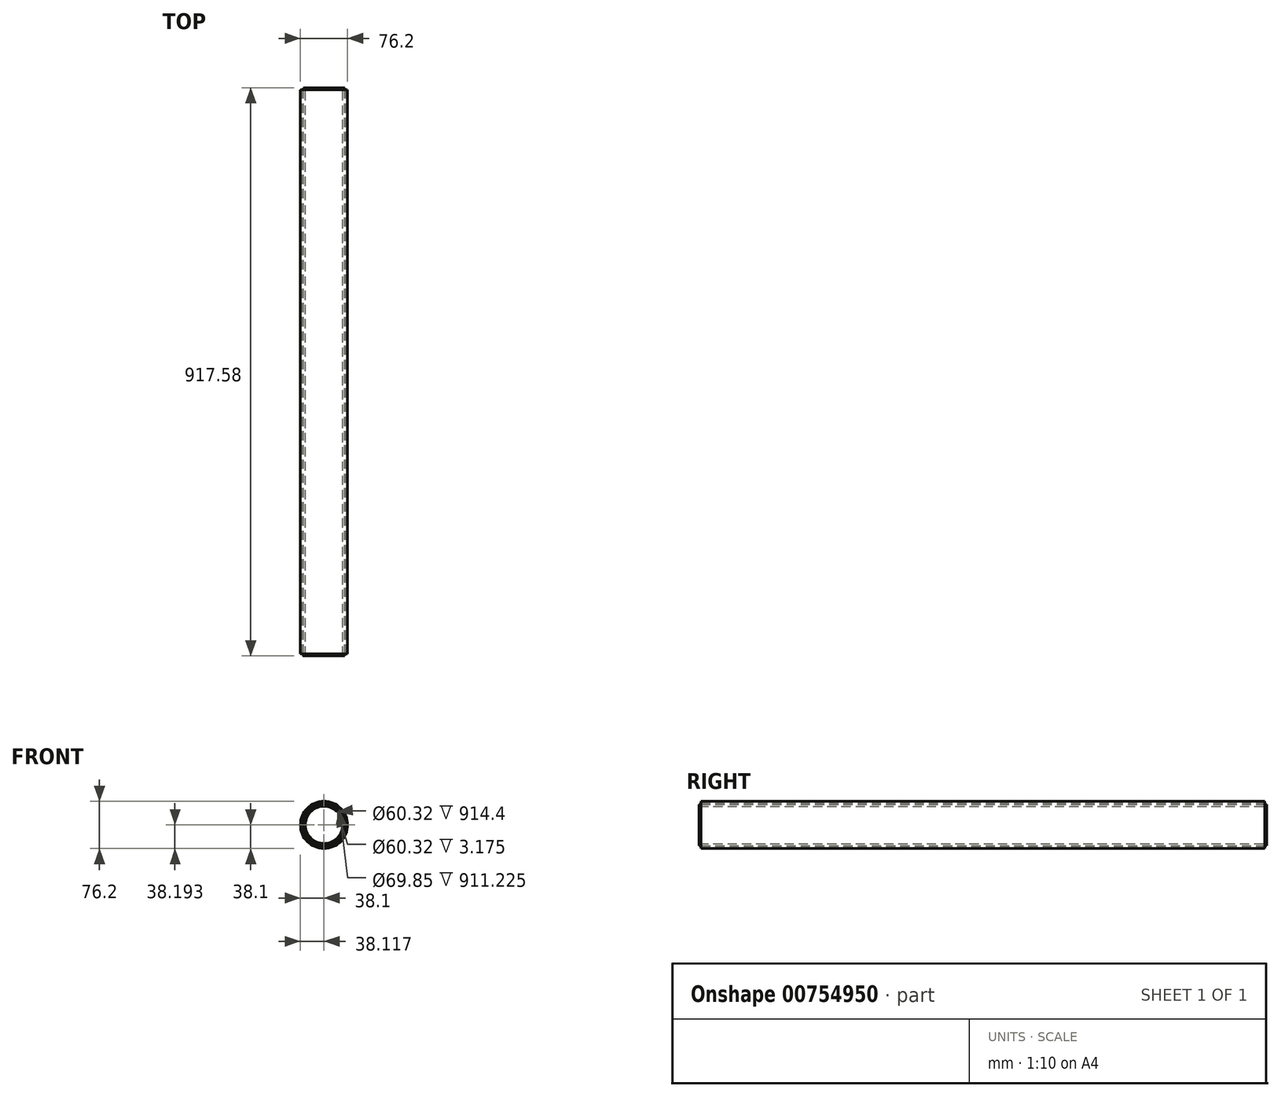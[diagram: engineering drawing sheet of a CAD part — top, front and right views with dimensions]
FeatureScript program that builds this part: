
annotation { "Feature Type Name" : "Feature", "Feature Type Description" : "" }
export const myFeature = defineFeature(function(context is Context, id is Id, definition is map)
    precondition{}
    {
        {
            var Q0;
            Q0=qCreatedBy(makeId("Front.planeOp"),FACE);
            var sketch = newSketch(context, id + "F0", { "sketchPlane" : qUnion([Q0])});
            skCircle(sketch, "E0", {"center": v(0, 0) * mm, "radius": 38.1 * mm});
            skCircle(sketch, "E1", {"center": v(0, 0) * mm, "radius": 34.93 * mm});
            skCircle(sketch, "E2", {"center": v(0, 0) * mm, "radius": 33.34 * mm});
            skCircle(sketch, "E3", {"center": v(0, 0) * mm, "radius": 30.16 * mm});
            skSolve(sketch);
        }
        {
            var Q0;
            Q0=makeQuery(id+"F0.imprint","IMPRINT",FACE,{"disambiguationData":[TD([[makeQuery(id+"F0.imprint","IMPRINT",EDGE,{"derivedFrom":sQuery(id+"F0.wireOp",EDGE,"E0")}),1.0]])]});
            extrude(context, id + "F1", {"entities" : qUnion([Q0]), "depth" : 911.22 * mm, "offsetDistance" : 25.4 * mm});
        }
        {
            var Q0;
            Q0=makeQuery(id+"F0.imprint","IMPRINT",FACE,{"disambiguationData":[TD([[makeQuery(id+"F0.imprint","IMPRINT",EDGE,{"derivedFrom":sQuery(id+"F0.wireOp",EDGE,"E2")}),1.0]])]});
            extrude(context, id + "F2", {"entities" : qUnion([Q0]), "depth" : 914.4 * mm, "offsetDistance" : 25.4 * mm});
        }
        {
            var Q0;
            Q0=qCreatedBy(makeId("Front.planeOp"),FACE);
            var sketch = newSketch(context, id + "F3", { "sketchPlane" : qUnion([Q0])});
            skCircle(sketch, "E4", {"center": v(0.02, 0.1) * mm, "radius": 33.34 * mm});
            skCircle(sketch, "E5", {"center": v(0.02, 0.1) * mm, "radius": 30.16 * mm});
            skSolve(sketch);
        }
        {
            var Q0;
            Q0=makeQuery(id+"F3.imprint","IMPRINT",FACE,{"disambiguationData":[TD([[makeQuery(id+"F3.imprint","IMPRINT",EDGE,{"derivedFrom":sQuery(id+"F3.wireOp",EDGE,"E4")}),1.0]])]});
            extrude(context, id + "F4", {"entities" : qUnion([Q0]), "operationType" : NewBodyOperationType.ADD, "oppositeDirection" : true, "depth" : 3.17 * mm, "offsetDistance" : 25.4 * mm});
        }
    });
